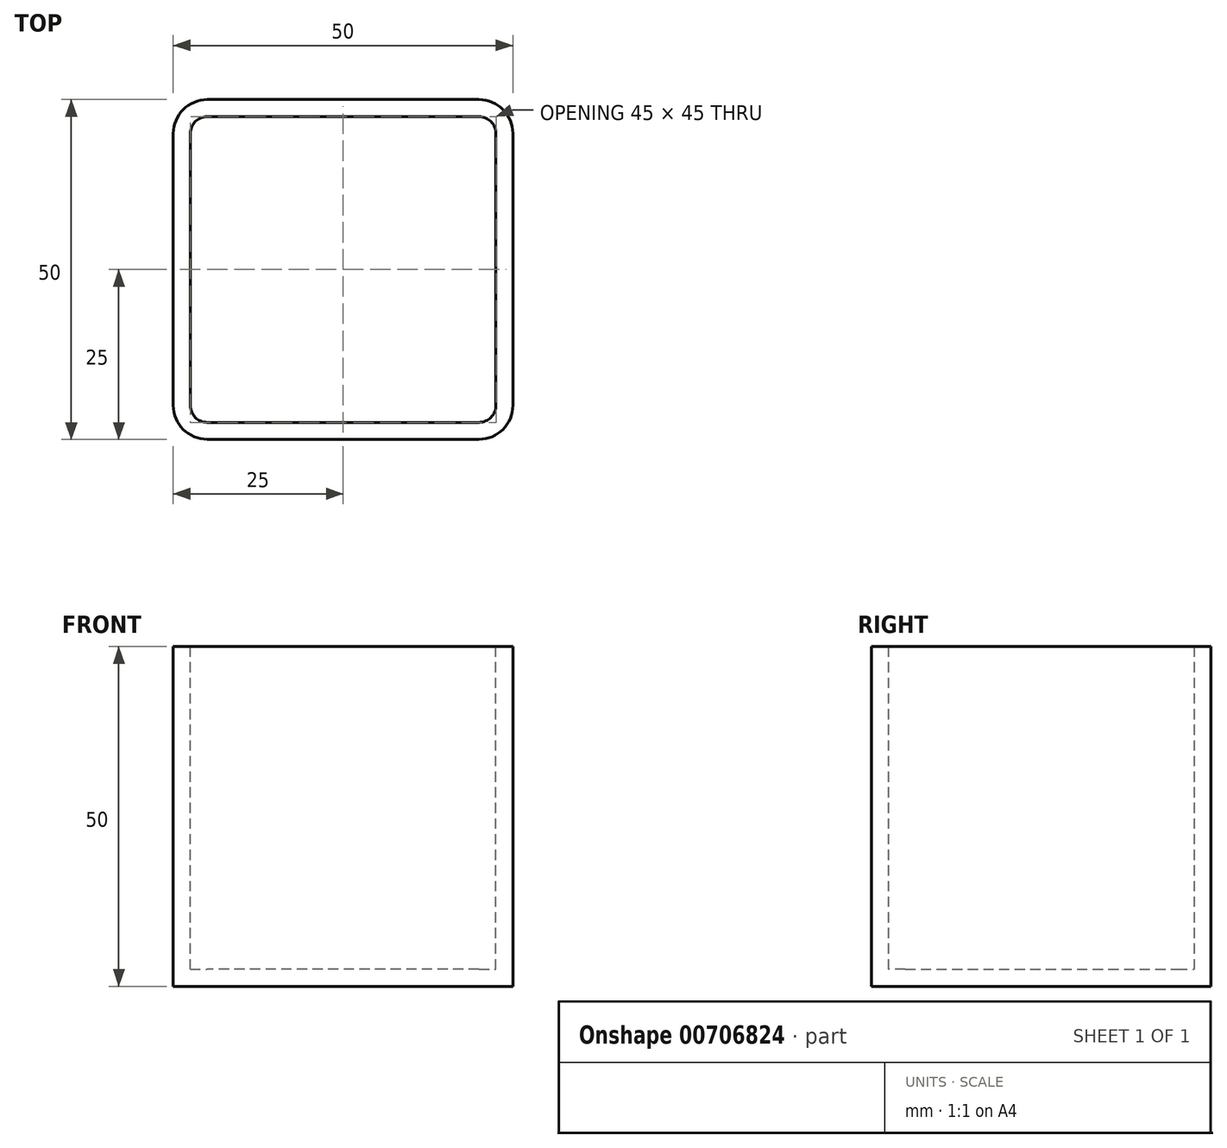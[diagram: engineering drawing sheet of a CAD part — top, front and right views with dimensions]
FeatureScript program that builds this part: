
annotation { "Feature Type Name" : "Feature", "Feature Type Description" : "" }
export const myFeature = defineFeature(function(context is Context, id is Id, definition is map)
    precondition{}
    {
        {
            var Q0;
            Q0=qCreatedBy(makeId("Top.planeOp"),FACE);
            var sketch = newSketch(context, id + "F0", { "sketchPlane" : qUnion([Q0])});
            skLineSegment(sketch, "E0.bottom", {"start": v(25, -25) * mm, "end": v(-25, -25) * mm});
            skLineSegment(sketch, "E0.top", {"start": v(25, 25) * mm, "end": v(-25, 25) * mm});
            skLineSegment(sketch, "E0.left", {"start": v(25, -25) * mm, "end": v(25, 25) * mm});
            skLineSegment(sketch, "E0.right", {"start": v(-25, -25) * mm, "end": v(-25, 25) * mm});
            skPoint(sketch, "E0.middle", {"position": v(0, 0) * mm});
            skSolve(sketch);
        }
        {
            var Q0;
            Q0=makeQuery(id+"F0.imprint","IMPRINT",FACE,{"disambiguationData":[TD([[makeQuery(id+"F0.imprint","IMPRINT",EDGE,{"derivedFrom":sQuery(id+"F0.wireOp",EDGE,"E0.bottom")}),-1.0]])]});
            extrude(context, id + "F1", {"entities" : qUnion([Q0]), "depth" : 50 * mm, "offsetDistance" : 25 * mm});
        }
        {
            var Q0;
            Q0=makeQuery(id+"F1.opExtrude","SWEPT_EDGE",EDGE,{"disambiguationData":[OSD([sQuery(id+"F0.wireOp",EDGE,"E0.bottom"),sQuery(id+"F0.wireOp",EDGE,"E0.left")])]});
            var Q1;
            Q1=makeQuery(id+"F1.opExtrude","SWEPT_EDGE",EDGE,{"disambiguationData":[OSD([sQuery(id+"F0.wireOp",EDGE,"E0.top"),sQuery(id+"F0.wireOp",EDGE,"E0.left")])]});
            var Q2;
            Q2=makeQuery(id+"F1.opExtrude","SWEPT_EDGE",EDGE,{"disambiguationData":[OSD([sQuery(id+"F0.wireOp",EDGE,"E0.bottom"),sQuery(id+"F0.wireOp",EDGE,"E0.right")])]});
            var Q3;
            Q3=makeQuery(id+"F1.opExtrude","SWEPT_EDGE",EDGE,{"disambiguationData":[OSD([sQuery(id+"F0.wireOp",EDGE,"E0.top"),sQuery(id+"F0.wireOp",EDGE,"E0.right")])]});
            fillet(context, id + "F2", {"entities" : qUnion([Q0, Q1, Q2, Q3]), "radius" : 5 * mm, "tangentPropagation" : true, "allowEdgeOverflow" : false});
        }
        {
            var Q0;
            Q0=makeQuery(id+"F1.opExtrude","CAP_FACE",FACE,{"disambiguationData":[OSD([sQuery(id+"F0.wireOp",EDGE,"E0.bottom"),sQuery(id+"F0.wireOp",EDGE,"E0.top"),sQuery(id+"F0.wireOp",EDGE,"E0.left"),sQuery(id+"F0.wireOp",EDGE,"E0.right")])],"isStart":false});
            shell(context, id + "F3", {"entities" : qUnion([Q0]), "thickness" : 2.5 * mm});
        }
    });
